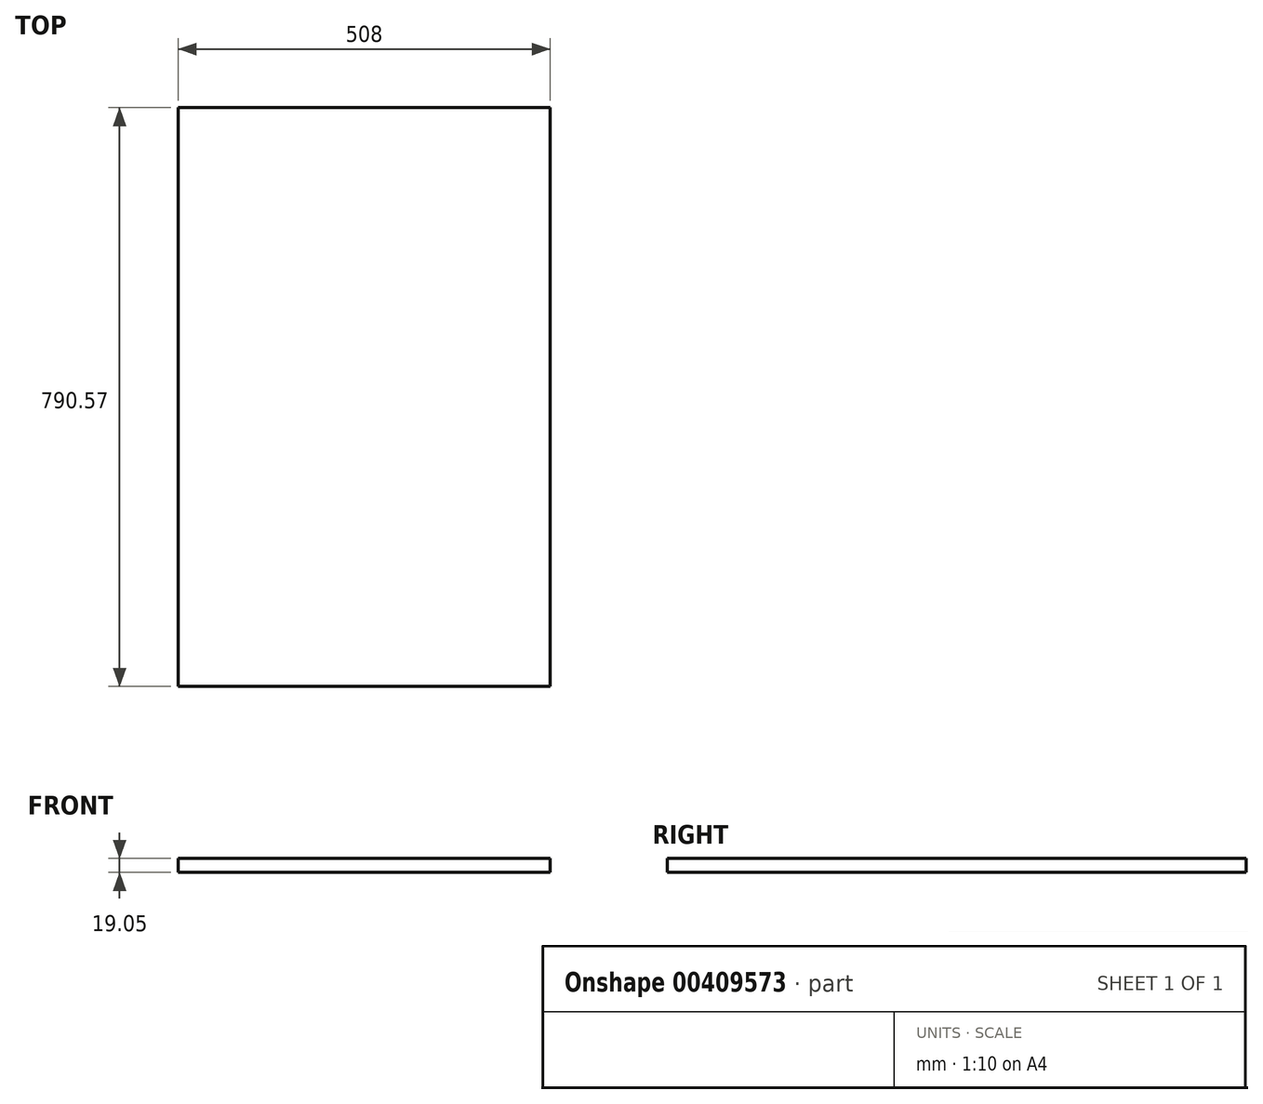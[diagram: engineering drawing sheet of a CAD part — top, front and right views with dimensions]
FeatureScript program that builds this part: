
annotation { "Feature Type Name" : "Feature", "Feature Type Description" : "" }
export const myFeature = defineFeature(function(context is Context, id is Id, definition is map)
    precondition{}
    {
        {
            var Q0;
            Q0=qCreatedBy(makeId("Top.planeOp"),FACE);
            var sketch = newSketch(context, id + "F0", { "sketchPlane" : qUnion([Q0])});
            skLineSegment(sketch, "E0.bottom", {"start": v(-383.84, 395.55) * mm, "end": v(124.16, 395.55) * mm});
            skLineSegment(sketch, "E0.top", {"start": v(-383.84, -395.02) * mm, "end": v(124.16, -395.02) * mm});
            skLineSegment(sketch, "E0.left", {"start": v(-383.84, 395.55) * mm, "end": v(-383.84, -395.02) * mm});
            skLineSegment(sketch, "E0.right", {"start": v(124.16, 395.55) * mm, "end": v(124.16, -395.02) * mm});
            skSolve(sketch);
        }
        {
            var Q0;
            Q0 = qSketchRegion(id + "F0", true);
            extrude(context, id + "F1", {"entities" : qUnion([Q0]), "depth" : 19.05 * mm});
        }
    });
